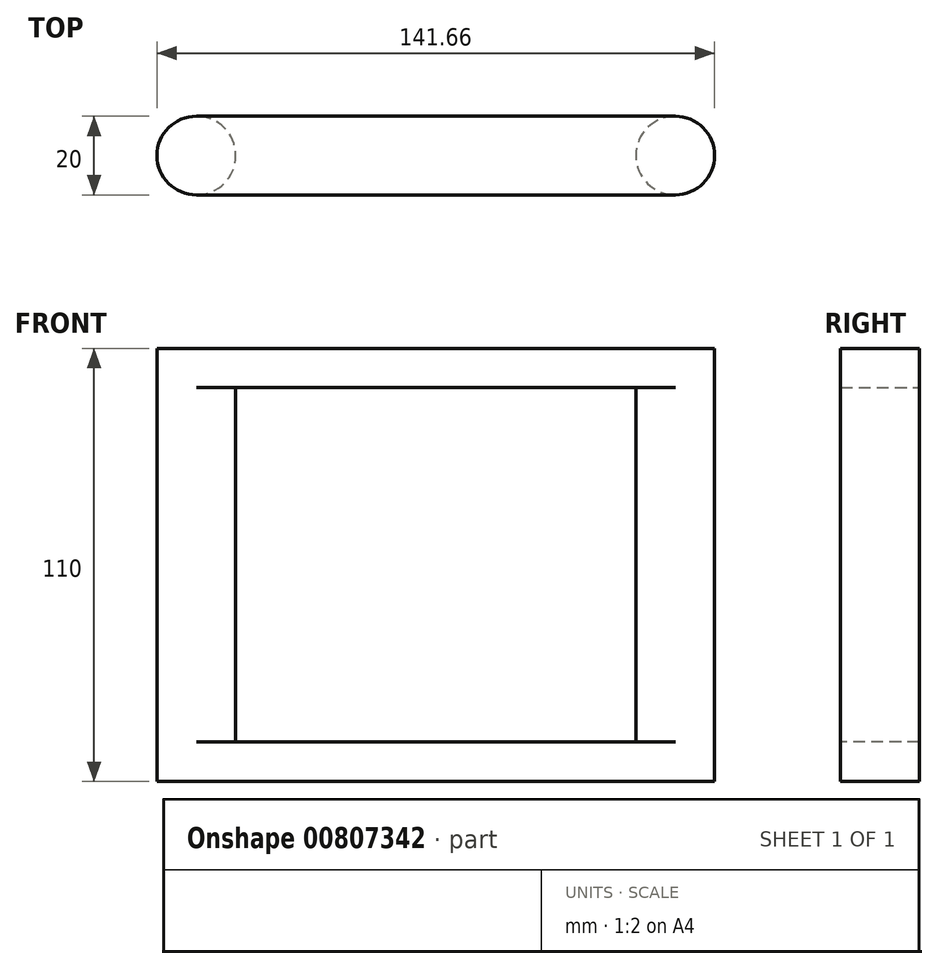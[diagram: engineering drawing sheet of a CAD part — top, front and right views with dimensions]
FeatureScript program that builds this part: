
annotation { "Feature Type Name" : "Feature", "Feature Type Description" : "" }
export const myFeature = defineFeature(function(context is Context, id is Id, definition is map)
    precondition{}
    {
        {
            var Q0;
            Q0=qCreatedBy(makeId("Front.planeOp"),FACE);
            var sketch = newSketch(context, id + "F0", { "sketchPlane" : qUnion([Q0])});
            skLineSegment(sketch, "E0", {"start": v(-71.66, 0) * mm, "end": v(70, 0) * mm});
            skLineSegment(sketch, "E1", {"start": v(-71.66, 0) * mm, "end": v(-71.66, -10) * mm});
            skLineSegment(sketch, "E2", {"start": v(-71.66, -10) * mm, "end": v(70, -10) * mm});
            skLineSegment(sketch, "E3", {"start": v(70, 0) * mm, "end": v(70, -10) * mm});
            skSolve(sketch);
        }
        {
            var Q0;
            Q0 = qSketchRegion(id + "F0", true);
            extrude(context, id + "F1", {"entities" : qUnion([Q0]), "depth" : 20 * mm, "offsetDistance" : 25 * mm});
        }
        {
            var Q0;
            Q0=makeQuery(id+"F1.opExtrude","SWEPT_FACE",FACE,{"disambiguationData":[OSD([sQuery(id+"F0.wireOp",EDGE,"E0")])]});
            var sketch = newSketch(context, id + "F2", { "sketchPlane" : qUnion([Q0])});
            skCircle(sketch, "E4", {"center": v(-61.66, -10) * mm, "radius": 10 * mm});
            skCircle(sketch, "E5", {"center": v(60, -10) * mm, "radius": 10 * mm});
            skSolve(sketch);
        }
        {
            var Q0;
            Q0 = qSketchRegion(id + "F2", true);
            extrude(context, id + "F3", {"entities" : qUnion([Q0]), "operationType" : NewBodyOperationType.ADD, "depth" : 90 * mm, "offsetDistance" : 25 * mm});
        }
        {
            var Q0;
            Q0=makeQuery(id+"F3.opExtrude","CAP_FACE",FACE,{"disambiguationData":[OSD([sQuery(id+"F2.wireOp",EDGE,"E4")])],"isStart":false});
            var sketch = newSketch(context, id + "F4", { "sketchPlane" : qUnion([Q0])});
            skLineSegment(sketch, "E6.bottom", {"start": v(-71.66, 0) * mm, "end": v(70, 0) * mm});
            skLineSegment(sketch, "E6.top", {"start": v(-71.66, -20) * mm, "end": v(70, -20) * mm});
            skLineSegment(sketch, "E6.left", {"start": v(-71.66, 0) * mm, "end": v(-71.66, -20) * mm});
            skLineSegment(sketch, "E6.right", {"start": v(70, 0) * mm, "end": v(70, -20) * mm});
            skSolve(sketch);
        }
        {
            var Q0;
            Q0 = qSketchRegion(id + "F4", true);
            extrude(context, id + "F5", {"entities" : qUnion([Q0]), "operationType" : NewBodyOperationType.ADD, "depth" : 10 * mm, "offsetDistance" : 25 * mm});
        }
        {
            var Q0;
            Q0=makeQuery(id+"F1.opExtrude","CAP_EDGE",EDGE,{"disambiguationData":[OSD([sQuery(id+"F0.wireOp",EDGE,"E1")])],"isStart":false});
            var Q1;
            Q1=makeQuery(id+"F1.opExtrude","CAP_EDGE",EDGE,{"disambiguationData":[OSD([sQuery(id+"F0.wireOp",EDGE,"E1")])],"isStart":true});
            var Q2;
            Q2=makeQuery(id+"F5.opExtrude","SWEPT_EDGE",EDGE,{"disambiguationData":[OSD([sQuery(id+"F4.wireOp",EDGE,"E6.top"),sQuery(id+"F4.wireOp",EDGE,"E6.left")])]});
            var Q3;
            Q3=makeQuery(id+"F5.opExtrude","SWEPT_EDGE",EDGE,{"disambiguationData":[OSD([sQuery(id+"F4.wireOp",EDGE,"E6.bottom"),sQuery(id+"F4.wireOp",EDGE,"E6.left")])]});
            var Q4;
            Q4=makeQuery(id+"F5.opExtrude","SWEPT_EDGE",EDGE,{"disambiguationData":[OSD([sQuery(id+"F4.wireOp",EDGE,"E6.bottom"),sQuery(id+"F4.wireOp",EDGE,"E6.right")])]});
            var Q5;
            Q5=makeQuery(id+"F5.opExtrude","SWEPT_EDGE",EDGE,{"disambiguationData":[OSD([sQuery(id+"F4.wireOp",EDGE,"E6.top"),sQuery(id+"F4.wireOp",EDGE,"E6.right")])]});
            var Q6;
            Q6=makeQuery(id+"F1.opExtrude","CAP_EDGE",EDGE,{"disambiguationData":[OSD([sQuery(id+"F0.wireOp",EDGE,"E3")])],"isStart":true});
            var Q7;
            Q7=makeQuery(id+"F1.opExtrude","CAP_EDGE",EDGE,{"disambiguationData":[OSD([sQuery(id+"F0.wireOp",EDGE,"E3")])],"isStart":false});
            fillet(context, id + "F6", {"entities" : qUnion([Q0, Q1, Q2, Q3, Q4, Q5, Q6, Q7]), "radius" : 10 * mm, "tangentPropagation" : true, "allowEdgeOverflow" : false});
        }
    });
